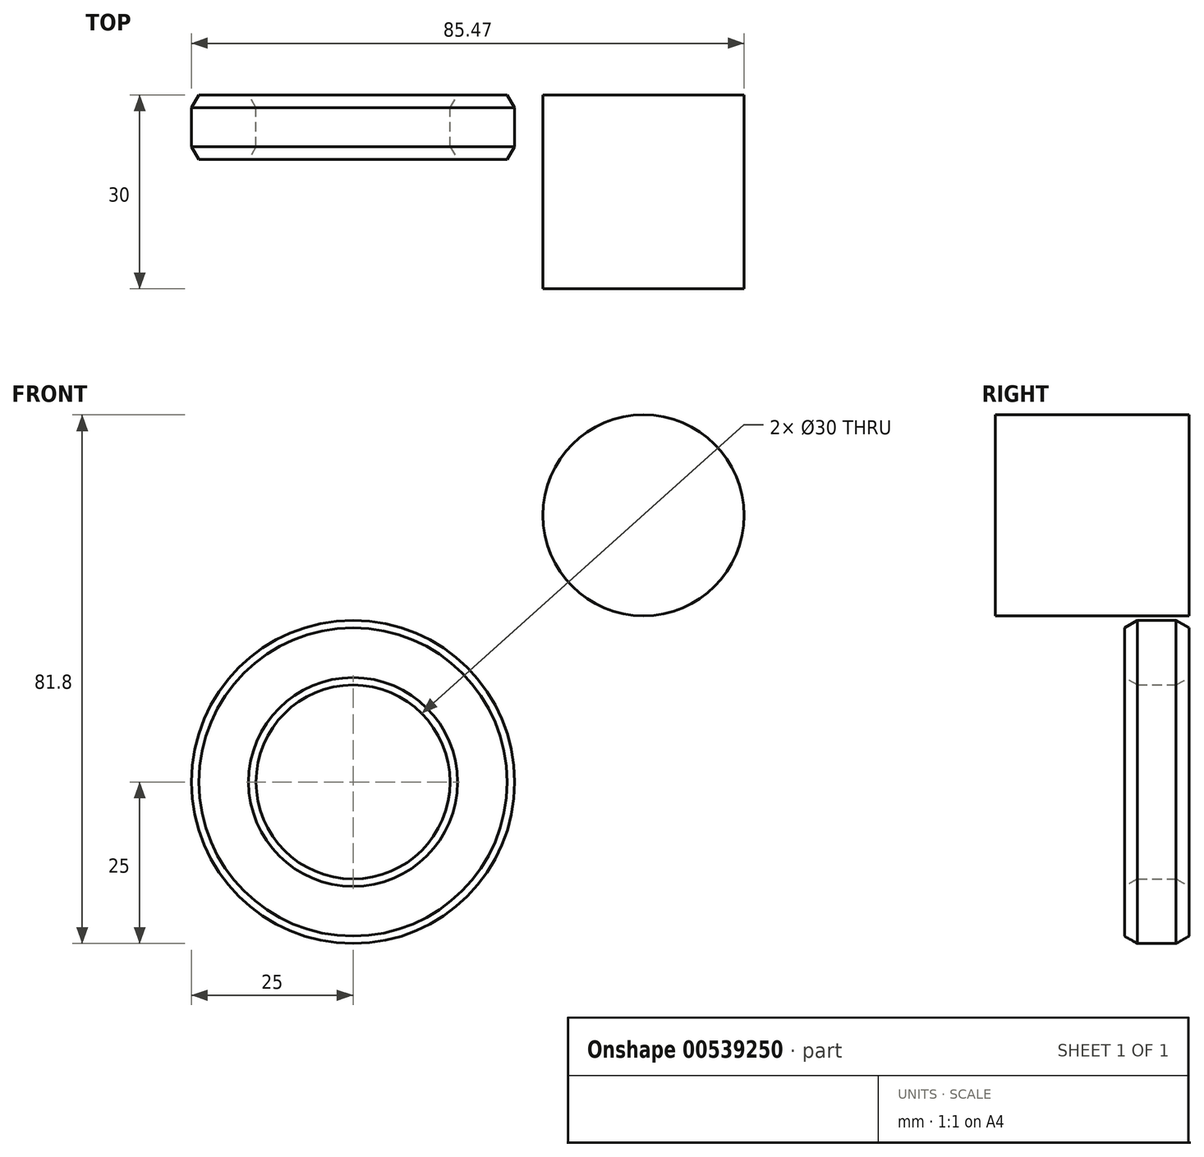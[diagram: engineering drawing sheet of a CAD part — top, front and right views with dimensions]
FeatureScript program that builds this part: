
annotation { "Feature Type Name" : "Feature", "Feature Type Description" : "" }
export const myFeature = defineFeature(function(context is Context, id is Id, definition is map)
    precondition{}
    {
        {
            var Q0;
            Q0=qCreatedBy(makeId("Front.planeOp"),FACE);
            var sketch = newSketch(context, id + "F0", { "sketchPlane" : qUnion([Q0])});
            skCircle(sketch, "E0", {"center": v(0, 0) * mm, "radius": 25 * mm});
            skCircle(sketch, "E1", {"center": v(0, 0) * mm, "radius": 15 * mm});
            skSolve(sketch);
        }
        {
            var Q0;
            Q0=makeQuery(id+"F0.imprint","IMPRINT",FACE,{"disambiguationData":[TD([[makeQuery(id+"F0.imprint","IMPRINT",EDGE,{"derivedFrom":sQuery(id+"F0.wireOp",EDGE,"E0")}),1.0]])]});
            extrude(context, id + "F1", {"entities" : qUnion([Q0]), "depth" : 10 * mm, "offsetDistance" : 25 * mm});
        }
        {
            var Q0;
            Q0=makeQuery(id+"F1.opExtrude","CAP_FACE",FACE,{"disambiguationData":[OSD([sQuery(id+"F0.wireOp",EDGE,"E0"),sQuery(id+"F0.wireOp",EDGE,"E1")])],"isStart":true});
            var Q1;
            Q1=makeQuery(id+"F1.opExtrude","CAP_FACE",FACE,{"disambiguationData":[OSD([sQuery(id+"F0.wireOp",EDGE,"E0"),sQuery(id+"F0.wireOp",EDGE,"E1")])],"isStart":false});
            chamfer(context, id + "F2", {"entities" : qUnion([Q0, Q1]), "chamferType" : ChamferType.OFFSET_ANGLE, "width" : 2 * mm, "oppositeDirection" : false, "angle" : 30 * degree, "tangentPropagation" : true});
        }
        {
            var Q0;
            Q0=qCreatedBy(makeId("Front.planeOp"),FACE);
            var sketch = newSketch(context, id + "F3", { "sketchPlane" : qUnion([Q0])});
            skCircle(sketch, "E2", {"center": v(44.92, 41.25) * mm, "radius": 15.55 * mm});
            skSolve(sketch);
        }
        {
            var Q0;
            Q0 = qSketchRegion(id + "F3", true);
            extrude(context, id + "F4", {"entities" : qUnion([Q0]), "depth" : 30 * mm, "offsetDistance" : 25 * mm});
        }
    });
